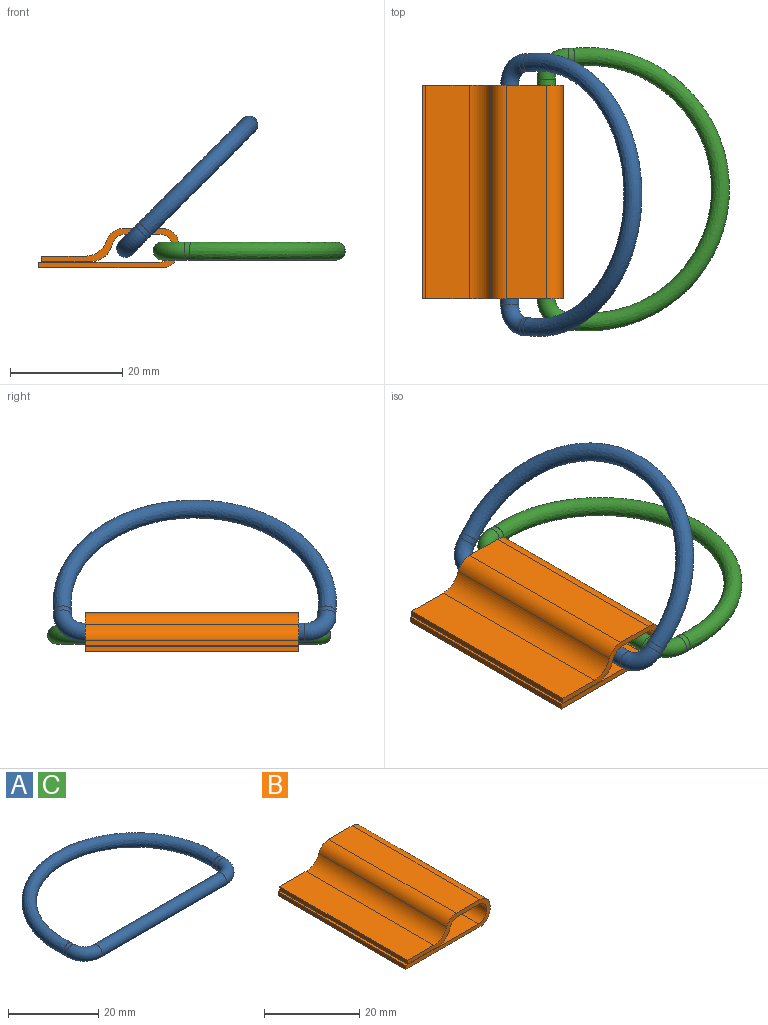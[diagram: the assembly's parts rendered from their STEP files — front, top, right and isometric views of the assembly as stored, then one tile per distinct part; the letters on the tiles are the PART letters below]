
ASSEMBLY  parts=3 mates=2
PART A: 6 faces, bbox 51.1x34.6x3.2 mm
  f0: torus R=4mm, axis (0,0,1), area 63.2mm2, adj f1,f3
  f1: cylinder r=1.6mm len=39mm, axis (1,0,0), area 392.1mm2, adj f0,f2
  f2: torus R=4mm, axis (0,0,1), area 63.2mm2, adj f1,f4
  f3: cylinder r=1.6mm len=3.2mm, axis (0,-1,0), area 10.1mm2, adj f0,f5
  f4: cylinder r=1.6mm len=3.2mm, axis (0,1,0), area 10.1mm2, adj f2,f5
  f5: bspline ~50.39x27.81mm, area 793.7mm2, adj f3,f4
PART B: 18 faces, bbox 25x38x7 mm
  f0: plane 38x8.7mm, normal (0,0,-1), area 330.6mm2, adj f8,f9,f10,f17
  f1: plane 38x6mm, normal (0,0,-1), area 228mm2, adj f9,f10,f11,f12
  f2: plane 38x21.5mm, normal (0,0,1), area 817mm2, adj f3,f9,f10,f12
  f3: plane 38x1mm, normal (-1,0,0), area 38mm2, adj f2,f4,f9,f10
  f4: plane 38x22mm, normal (0,0,-1), area 836mm2, adj f3,f9,f10,f15
  f5: plane 38x1mm, normal (1,0,0), area 38mm2, adj f9,f10,f14,f15
  f6: plane 38x7mm, normal (0,0,1), area 266mm2, adj f9,f10,f13,f14
  f7: plane 38x7.82mm, normal (0,0,1), area 297.3mm2, adj f8,f9,f10,f16
  f8: plane 38x1mm, normal (-1,0,0), area 38mm2, adj f0,f7,f9,f10
  f9: plane 25x7mm, normal (0,-1,0), area 57.3mm2, adj f0,f1,f2,f3,f4,f5,f6,f7
  f10: plane 25x7mm, normal (0,1,0), area 57.3mm2, adj f0,f1,f2,f3,f4,f5,f6,f7
  f11: cylinder r=2.5mm len=38mm, axis (0,-1,0), area 125.6mm2, adj f1,f9,f10,f17
  f12: cylinder r=2.5mm len=38mm, axis (0,-1,0), area 298.5mm2, adj f1,f2,f9,f10
  f13: cylinder r=3mm len=38mm, axis (0,1,0), area 144.3mm2, adj f6,f9,f10,f16
  f14: cylinder r=3mm len=38mm, axis (0,1,0), area 179.1mm2, adj f5,f6,f9,f10
  f15: cylinder r=3mm len=38mm, axis (0,1,0), area 179.1mm2, adj f4,f5,f9,f10
  f16: cylinder r=4mm len=38mm, axis (0,1,0), area 192.4mm2, adj f7,f9,f10,f13
  f17: cylinder r=4mm len=38mm, axis (0,-1,0), area 201mm2, adj f0,f9,f10,f11
PART C: same geometry as A
PLACE A rot(axis=(0.36,-0.36,-0.86),98.4deg) t=(-19.93,-23.97,0.01)mm
PLACE B t=(-35.43,-4.47,-3.49)mm
PLACE C rot(axis=(0,0,-1),90deg) t=(-13.43,-22.97,-0.49)mm
MATE fastened A.f1 <-> B.f11  axis (0,-1,0) through (-19.93,-43.47,0.01)mm
MATE fastened C.f1 <-> B.f15  axis (0,-1,0) through (-13.43,-42.47,-0.49)mm
